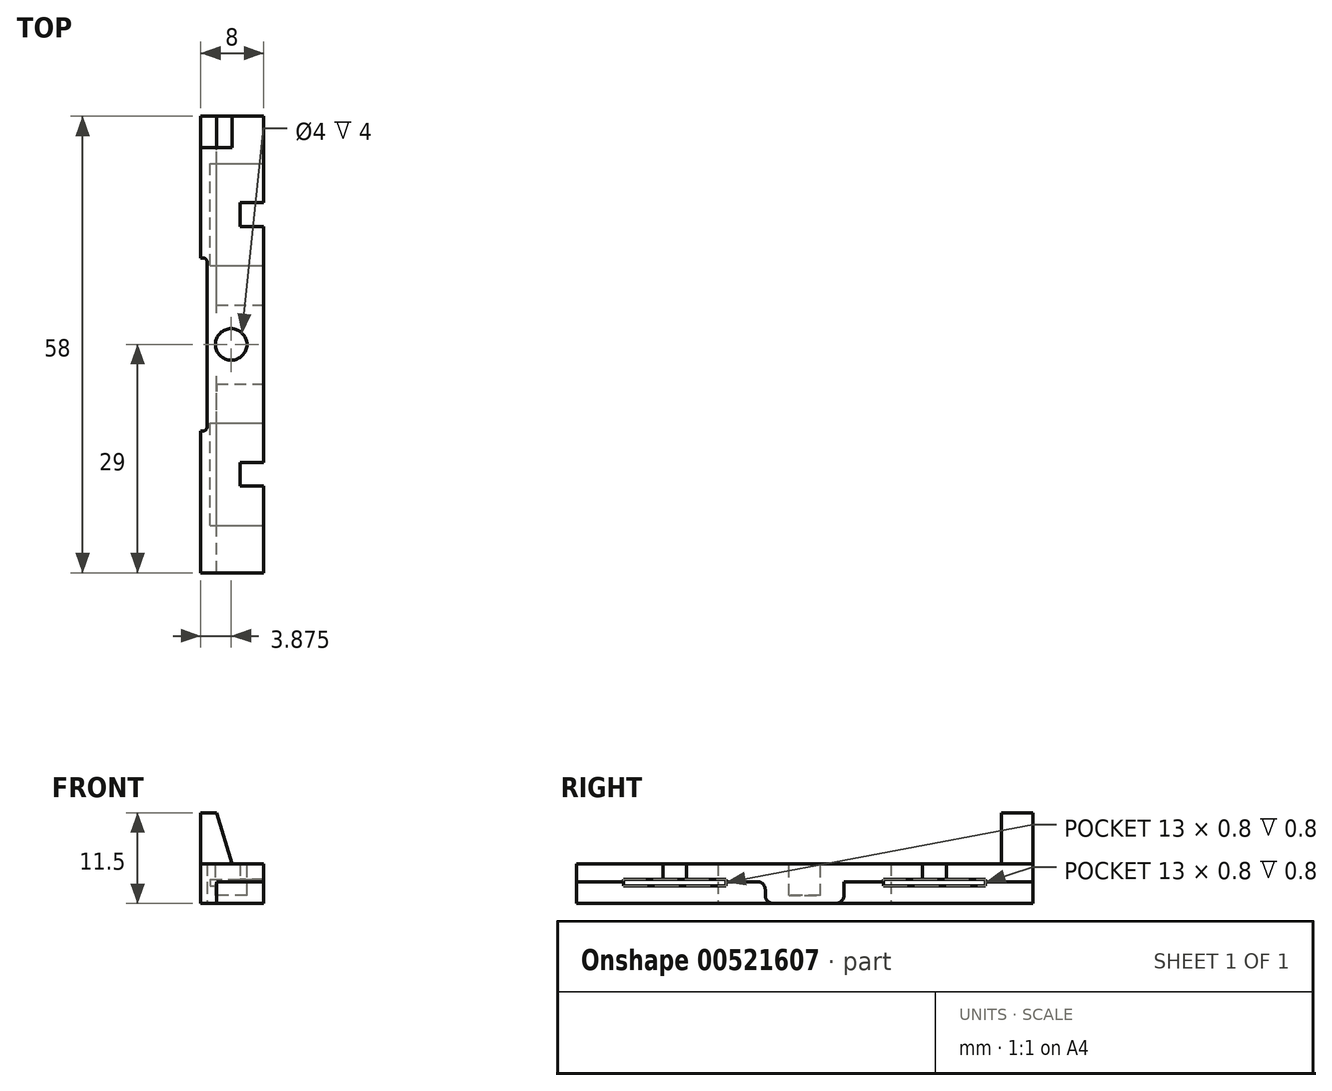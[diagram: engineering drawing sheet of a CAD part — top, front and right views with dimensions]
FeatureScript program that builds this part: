
annotation { "Feature Type Name" : "Feature", "Feature Type Description" : "" }
export const myFeature = defineFeature(function(context is Context, id is Id, definition is map)
    precondition{}
    {
        {
            var Q0;
            Q0=qCreatedBy(makeId("Right.planeOp"),FACE);
            var sketch = newSketch(context, id + "F0", { "sketchPlane" : qUnion([Q0])});
            skLineSegment(sketch, "E0.bottom", {"start": v(-29, 2.5) * mm, "end": v(29, 2.5) * mm});
            skLineSegment(sketch, "E0.top", {"start": v(-29, -2.5) * mm, "end": v(29, -2.5) * mm});
            skLineSegment(sketch, "E0.left", {"start": v(-29, 2.5) * mm, "end": v(-29, -2.5) * mm});
            skLineSegment(sketch, "E0.right", {"start": v(29, 2.5) * mm, "end": v(29, -2.5) * mm});
            skPoint(sketch, "E0.middle", {"position": v(0, 0) * mm});
            skSolve(sketch);
        }
        {
            var Q0;
            Q0 = qSketchRegion(id + "F0", true);
            extrude(context, id + "F1", {"entities" : qUnion([Q0]), "depth" : 2 * mm, "offsetDistance" : 25 * mm});
        }
        {
            var Q0;
            Q0=makeQuery(id+"F1.opExtrude","CAP_FACE",FACE,{"disambiguationData":[OSD([sQuery(id+"F0.wireOp",EDGE,"E0.bottom"),sQuery(id+"F0.wireOp",EDGE,"E0.top"),sQuery(id+"F0.wireOp",EDGE,"E0.left"),sQuery(id+"F0.wireOp",EDGE,"E0.right")])],"isStart":false});
            var sketch = newSketch(context, id + "F2", { "sketchPlane" : qUnion([Q0])});
            skLineSegment(sketch, "E1.bottom", {"start": v(10, 0.25) * mm, "end": v(23, 0.25) * mm});
            skLineSegment(sketch, "E1.top", {"start": v(10, -0.25) * mm, "end": v(23, -0.25) * mm});
            skLineSegment(sketch, "E1.left", {"start": v(10, 0.25) * mm, "end": v(10, -0.25) * mm});
            skLineSegment(sketch, "E1.right", {"start": v(23, 0.25) * mm, "end": v(23, -0.25) * mm});
            skPoint(sketch, "E1.middle", {"position": v(16.5, 0) * mm});
            skLineSegment(sketch, "E2.bottom", {"start": v(-23, 0.25) * mm, "end": v(-10, 0.25) * mm});
            skLineSegment(sketch, "E2.top", {"start": v(-23, -0.25) * mm, "end": v(-10, -0.25) * mm});
            skLineSegment(sketch, "E2.left", {"start": v(-23, 0.25) * mm, "end": v(-23, -0.25) * mm});
            skLineSegment(sketch, "E2.right", {"start": v(-10, 0.25) * mm, "end": v(-10, -0.25) * mm});
            skPoint(sketch, "E2.middle", {"position": v(-16.5, 0) * mm});
            skSolve(sketch);
        }
        {
            var Q0;
            Q0 = qSketchRegion(id + "F2", true);
            extrude(context, id + "F3", {"entities" : qUnion([Q0]), "operationType" : NewBodyOperationType.REMOVE, "oppositeDirection" : true, "depth" : .8 * mm, "offsetDistance" : 25 * mm});
        }
        {
            var Q0;
            Q0=makeQuery(id+"F1.opExtrude","CAP_FACE",FACE,{"disambiguationData":[OSD([sQuery(id+"F0.wireOp",EDGE,"E0.bottom"),sQuery(id+"F0.wireOp",EDGE,"E0.top"),sQuery(id+"F0.wireOp",EDGE,"E0.left"),sQuery(id+"F0.wireOp",EDGE,"E0.right")])],"isStart":false});
            var sketch = newSketch(context, id + "F4", { "sketchPlane" : qUnion([Q0])});
            skPoint(sketch, "E3.oppositeSnap0", {"position": v(-16.5, 0.25) * mm});
            skLineSegment(sketch, "E3.bottom", {"start": v(-29, 2.5) * mm, "end": v(29, 2.5) * mm});
            skLineSegment(sketch, "E3.top", {"start": v(-29, 0.25) * mm, "end": v(29, 0.25) * mm});
            skLineSegment(sketch, "E3.left", {"start": v(-29, 2.5) * mm, "end": v(-29, 0.25) * mm});
            skLineSegment(sketch, "E3.right", {"start": v(29, 2.5) * mm, "end": v(29, 0.25) * mm});
            skSolve(sketch);
        }
        {
            var Q0;
            Q0 = qSketchRegion(id + "F4", true);
            extrude(context, id + "F5", {"entities" : qUnion([Q0]), "operationType" : NewBodyOperationType.ADD, "depth" : 6 * mm, "offsetDistance" : 25 * mm});
        }
        {
            var Q0;
            Q0=makeQuery(id+"F5.boolean.opBoolean","MERGE",FACE,{"derivedFrom":[makeQuery(id+"F3.boolean.opBoolean","COPY",FACE,{"derivedFrom":makeQuery(id+"F3.opExtrude","SWEPT_FACE",FACE,{"disambiguationData":[OSD([sQuery(id+"F2.wireOp",EDGE,"E1.bottom")])]})}),makeQuery(id+"F3.boolean.opBoolean","COPY",FACE,{"derivedFrom":makeQuery(id+"F3.opExtrude","SWEPT_FACE",FACE,{"disambiguationData":[OSD([sQuery(id+"F2.wireOp",EDGE,"E2.bottom")])]})}),makeQuery(id+"F5.opExtrude","SWEPT_FACE",FACE,{"disambiguationData":[OSD([sQuery(id+"F4.wireOp",EDGE,"E3.top")])]})]});
            var sketch = newSketch(context, id + "F6", { "sketchPlane" : qUnion([Q0])});
            skLineSegment(sketch, "E4.bottom", {"start": v(2, 5) * mm, "end": v(8, 5) * mm});
            skLineSegment(sketch, "E4.top", {"start": v(2, -5) * mm, "end": v(8, -5) * mm});
            skLineSegment(sketch, "E4.left", {"start": v(2, 5) * mm, "end": v(2, -5) * mm});
            skLineSegment(sketch, "E4.right", {"start": v(8, 5) * mm, "end": v(8, -5) * mm});
            skPoint(sketch, "E4.middle", {"position": v(5, 0) * mm});
            skSolve(sketch);
        }
        {
            var Q0;
            Q0=makeQuery(id+"F6.imprint","IMPRINT",FACE,{"disambiguationData":[TD([[makeQuery(id+"F6.imprint","IMPRINT",EDGE,{"derivedFrom":sQuery(id+"F6.wireOp",EDGE,"E4.bottom")}),-1.0]])]});
            var Q1;
            Q1=makeQuery(id+"F1.opExtrude","SWEPT_FACE",FACE,{"disambiguationData":[OSD([sQuery(id+"F0.wireOp",EDGE,"E0.top")])]});
            extrude(context, id + "F7", {"entities" : qUnion([Q0]), "operationType" : NewBodyOperationType.ADD, "endBound" : BoundingType.UP_TO_SURFACE, "depth" : 25 * mm, "endBoundEntityFace" : qUnion([Q1]), "offsetDistance" : 25 * mm});
        }
        {
            var Q0;
            Q0=makeQuery(id+"F5.boolean.opBoolean","MERGE",FACE,{"derivedFrom":[makeQuery(id+"F1.opExtrude","SWEPT_FACE",FACE,{"disambiguationData":[OSD([sQuery(id+"F0.wireOp",EDGE,"E0.bottom")])]}),makeQuery(id+"F5.opExtrude","SWEPT_FACE",FACE,{"disambiguationData":[OSD([sQuery(id+"F4.wireOp",EDGE,"E3.bottom")])]})]});
            var sketch = newSketch(context, id + "F8", { "sketchPlane" : qUnion([Q0])});
            skCircle(sketch, "E5", {"center": v(3.88, 0) * mm, "radius": 2 * mm});
            skSolve(sketch);
        }
        {
            var Q0;
            Q0 = qSketchRegion(id + "F8", true);
            extrude(context, id + "F9", {"entities" : qUnion([Q0]), "operationType" : NewBodyOperationType.REMOVE, "oppositeDirection" : true, "depth" : 4 * mm, "offsetDistance" : 25 * mm});
        }
        {
            var Q0;
            Q0=makeQuery(id+"F7.opExtrude","CAP_EDGE",EDGE,{"disambiguationData":[OSD([sQuery(id+"F6.wireOp",EDGE,"E4.bottom")])],"isStart":false});
            var Q1;
            Q1=makeQuery(id+"F7.opExtrude","CAP_EDGE",EDGE,{"disambiguationData":[OSD([sQuery(id+"F6.wireOp",EDGE,"E4.bottom")])],"isStart":true});
            var Q2;
            Q2=makeQuery(id+"F7.opExtrude","CAP_EDGE",EDGE,{"disambiguationData":[OSD([sQuery(id+"F6.wireOp",EDGE,"E4.top")])],"isStart":true});
            var Q3;
            Q3=makeQuery(id+"F7.opExtrude","CAP_EDGE",EDGE,{"disambiguationData":[OSD([sQuery(id+"F6.wireOp",EDGE,"E4.top")])],"isStart":false});
            fillet(context, id + "F10", {"entities" : qUnion([Q0, Q1, Q2, Q3]), "radius" : 1 * mm, "tangentPropagation" : true, "allowEdgeOverflow" : false});
        }
        {
            var Q0;
            Q0=makeQuery(id+"F5.boolean.opBoolean","MERGE",FACE,{"derivedFrom":[makeQuery(id+"F1.opExtrude","SWEPT_FACE",FACE,{"disambiguationData":[OSD([sQuery(id+"F0.wireOp",EDGE,"E0.right")])]}),makeQuery(id+"F5.opExtrude","SWEPT_FACE",FACE,{"disambiguationData":[OSD([sQuery(id+"F4.wireOp",EDGE,"E3.right")])]})]});
            var sketch = newSketch(context, id + "F11", { "sketchPlane" : qUnion([Q0])});
            skLineSegment(sketch, "E6", {"start": v(0, 2.5) * mm, "end": v(0, 9) * mm});
            skLineSegment(sketch, "E7", {"start": v(0, 9) * mm, "end": v(-2, 9) * mm});
            skLineSegment(sketch, "E8", {"start": v(-2, 9) * mm, "end": v(-4, 2.5) * mm});
            skLineSegment(sketch, "E9", {"start": v(-4, 2.5) * mm, "end": v(0, 2.5) * mm});
            skSolve(sketch);
        }
        {
            var Q0;
            Q0=makeQuery(id+"F11.imprint","IMPRINT",FACE,{"disambiguationData":[TD([[makeQuery(id+"F11.imprint","IMPRINT",EDGE,{"derivedFrom":sQuery(id+"F11.wireOp",EDGE,"E6")}),1.0]])]});
            extrude(context, id + "F12", {"entities" : qUnion([Q0]), "operationType" : NewBodyOperationType.ADD, "oppositeDirection" : true, "depth" : 4 * mm, "offsetDistance" : 25 * mm});
        }
        {
            var Q0;
            {var subQ0=sQuery(id+"F11.wireOp",EDGE,"E6");Q0=makeQuery(id+"Fv3bD8ehhflkk99_1.1.F12.boolean.opBoolean","MERGE",FACE,{"derivedFrom":[makeQuery(id+"F12.boolean.opBoolean","MERGE",FACE,{"derivedFrom":[makeQuery(id+"F1.opExtrude","CAP_FACE",FACE,{"disambiguationData":[OSD([sQuery(id+"F0.wireOp",EDGE,"E0.bottom"),sQuery(id+"F0.wireOp",EDGE,"E0.top"),sQuery(id+"F0.wireOp",EDGE,"E0.left"),sQuery(id+"F0.wireOp",EDGE,"E0.right")])],"isStart":true}),makeQuery(id+"F12.opExtrude","SWEPT_FACE",FACE,{"disambiguationData":[OSD([subQ0])]})]}),makeQuery(id+"Fv3bD8ehhflkk99_1.1.F12.opExtrude","SWEPT_FACE",FACE,{"disambiguationData":[OSD([subQ0])]})]});}
            var sketch = newSketch(context, id + "F13", { "sketchPlane" : qUnion([Q0])});
            skLineSegment(sketch, "E10.bottom", {"start": v(-11, 2.5) * mm, "end": v(11, 2.5) * mm});
            skLineSegment(sketch, "E10.top", {"start": v(-11, -2.5) * mm, "end": v(11, -2.5) * mm});
            skLineSegment(sketch, "E10.left", {"start": v(-11, 2.5) * mm, "end": v(-11, -2.5) * mm});
            skLineSegment(sketch, "E10.right", {"start": v(11, 2.5) * mm, "end": v(11, -2.5) * mm});
            skPoint(sketch, "E10.middle", {"position": v(0, 0) * mm});
            skSolve(sketch);
        }
        {
            var Q0;
            Q0=makeQuery(id+"F13.imprint","IMPRINT",FACE,{"disambiguationData":[TD([[makeQuery(id+"F13.imprint","IMPRINT",EDGE,{"derivedFrom":sQuery(id+"F13.wireOp",EDGE,"E10.bottom")}),1.0]])]});
            extrude(context, id + "F14", {"entities" : qUnion([Q0]), "operationType" : NewBodyOperationType.REMOVE, "oppositeDirection" : true, "depth" : .8 * mm, "offsetDistance" : 25 * mm});
        }
        {
            var Q0;
            {var subQ0=sQuery(id+"F0.wireOp",EDGE,"E0.top");var subQ1=sQuery(id+"F13.wireOp",EDGE,"E10.left");Q0=makeQuery(id+"F14.boolean.opBoolean","COPY",EDGE,{"disambiguationData":[TD([makeQuery(id+"F1.opExtrude","SWEPT_FACE",FACE,{"disambiguationData":[OSD([subQ0])]})])],"derivedFrom":makeQuery(id+"F14.opExtrude","CAP_EDGE",EDGE,{"disambiguationData":[OSD([subQ1])],"isStart":false})});}
            var Q1;
            {var subQ0=sQuery(id+"F13.wireOp",EDGE,"E10.left");Q1=makeQuery(id+"F14.boolean.opBoolean","COPY",EDGE,{"disambiguationData":[TD([makeQuery(id+"F1.opExtrude","SWEPT_FACE",FACE,{"disambiguationData":[OSD([sQuery(id+"F0.wireOp",EDGE,"E0.bottom")])]})])],"derivedFrom":makeQuery(id+"F14.opExtrude","CAP_EDGE",EDGE,{"disambiguationData":[OSD([subQ0])],"isStart":false})});}
            var Q2;
            {var subQ0=sQuery(id+"F13.wireOp",EDGE,"E10.right");Q2=makeQuery(id+"F14.boolean.opBoolean","COPY",EDGE,{"disambiguationData":[TD([makeQuery(id+"F1.opExtrude","SWEPT_FACE",FACE,{"disambiguationData":[OSD([sQuery(id+"F0.wireOp",EDGE,"E0.bottom")])]})])],"derivedFrom":makeQuery(id+"F14.opExtrude","CAP_EDGE",EDGE,{"disambiguationData":[OSD([subQ0])],"isStart":false})});}
            var Q3;
            {var subQ0=sQuery(id+"F0.wireOp",EDGE,"E0.top");var subQ1=sQuery(id+"F13.wireOp",EDGE,"E10.right");Q3=makeQuery(id+"F14.boolean.opBoolean","COPY",EDGE,{"disambiguationData":[TD([makeQuery(id+"F1.opExtrude","SWEPT_FACE",FACE,{"disambiguationData":[OSD([subQ0])]})])],"derivedFrom":makeQuery(id+"F14.opExtrude","CAP_EDGE",EDGE,{"disambiguationData":[OSD([subQ1])],"isStart":false})});}
            var Q4;
            Q4=makeQuery(id+"Fv3bD8ehhflkk99_1.1.F12.opExtrude","SWEPT_EDGE",EDGE,{"disambiguationData":[OSD([sQuery(id+"F0.wireOp",EDGE,"E0.bottom"),sQuery(id+"F0.wireOp",EDGE,"E0.right"),sQuery(id+"F4.wireOp",EDGE,"E3.bottom"),sQuery(id+"F4.wireOp",EDGE,"E3.right"),sQuery(id+"F11.wireOp",EDGE,"E8"),sQuery(id+"F11.wireOp",EDGE,"E9")])]});
            var Q5;
            Q5=makeQuery(id+"Fv3bD8ehhflkk99_1.1.F12.opExtrude","CAP_EDGE",EDGE,{"disambiguationData":[OSD([sQuery(id+"F11.wireOp",EDGE,"E9")])],"isStart":false});
            var Q6;
            Q6=makeQuery(id+"F12.opExtrude","SWEPT_EDGE",EDGE,{"disambiguationData":[OSD([sQuery(id+"F0.wireOp",EDGE,"E0.bottom"),sQuery(id+"F0.wireOp",EDGE,"E0.right"),sQuery(id+"F4.wireOp",EDGE,"E3.bottom"),sQuery(id+"F4.wireOp",EDGE,"E3.right"),sQuery(id+"F11.wireOp",EDGE,"E8"),sQuery(id+"F11.wireOp",EDGE,"E9")])]});
            var Q7;
            Q7=makeQuery(id+"F12.opExtrude","CAP_EDGE",EDGE,{"disambiguationData":[OSD([sQuery(id+"F11.wireOp",EDGE,"E9")])],"isStart":false});
            fillet(context, id + "F15", {"entities" : qUnion([Q0, Q1, Q2, Q3, Q4, Q5, Q6, Q7]), "radius" : .5 * mm, "tangentPropagation" : true, "allowEdgeOverflow" : false});
        }
        {
            var Q0;
            {var subQ2=sQuery(id+"F2.wireOp",EDGE,"E2.bottom");var subQ3=sQuery(id+"F0.wireOp",EDGE,"E0.left");var subQ5=sQuery(id+"F4.wireOp",EDGE,"E3.top");Q0=makeQuery(id+"F7.boolean.opBoolean","SPLIT",FACE,{"disambiguationData":[TD([makeQuery(id+"F1.opExtrude","SWEPT_FACE",FACE,{"disambiguationData":[OSD([subQ3])]})])],"derivedFrom":makeQuery(id+"F5.boolean.opBoolean","MERGE",FACE,{"derivedFrom":[makeQuery(id+"F3.boolean.opBoolean","COPY",FACE,{"derivedFrom":makeQuery(id+"F3.opExtrude","SWEPT_FACE",FACE,{"disambiguationData":[OSD([sQuery(id+"F2.wireOp",EDGE,"E1.bottom")])]})}),makeQuery(id+"F3.boolean.opBoolean","COPY",FACE,{"derivedFrom":makeQuery(id+"F3.opExtrude","SWEPT_FACE",FACE,{"disambiguationData":[OSD([subQ2])]})}),makeQuery(id+"F5.opExtrude","SWEPT_FACE",FACE,{"disambiguationData":[OSD([subQ5])]})]})});}
            var sketch = newSketch(context, id + "F16", { "sketchPlane" : qUnion([Q0])});
            skLineSegment(sketch, "E11.bottom", {"start": v(1.2, 23) * mm, "end": v(8, 23) * mm});
            skLineSegment(sketch, "E11.top", {"start": v(1.2, 10) * mm, "end": v(8, 10) * mm});
            skLineSegment(sketch, "E11.right", {"start": v(8, 23) * mm, "end": v(8, 10) * mm});
            skLineSegment(sketch, "E12.top", {"start": v(1.2, -23) * mm, "end": v(8, -23) * mm});
            skLineSegment(sketch, "E12.left", {"start": v(1.2, -10) * mm, "end": v(1.2, -23) * mm});
            skLineSegment(sketch, "E12.right", {"start": v(8, -10) * mm, "end": v(8, -23) * mm});
            skLineSegment(sketch, "E13", {"start": v(1.2, -10) * mm, "end": v(8, -10) * mm});
            skLineSegment(sketch, "E14", {"start": v(1.2, 23) * mm, "end": v(1.2, 10) * mm});
            skSolve(sketch);
        }
        {
            var Q0;
            Q0 = qSketchRegion(id + "F16", true);
            extrude(context, id + "F17", {"entities" : qUnion([Q0]), "operationType" : NewBodyOperationType.REMOVE, "oppositeDirection" : true, "depth" : .3 * mm, "offsetDistance" : 25 * mm});
        }
        {
            var Q0;
            Q0=makeQuery(id+"F17.boolean.opBoolean","COPY",FACE,{"derivedFrom":makeQuery(id+"F17.opExtrude","CAP_FACE",FACE,{"disambiguationData":[OSD([sQuery(id+"F16.wireOp",EDGE,"E12.top"),sQuery(id+"F16.wireOp",EDGE,"E12.left"),sQuery(id+"F16.wireOp",EDGE,"E12.right"),sQuery(id+"F16.wireOp",EDGE,"E13")])],"isStart":false})});
            var sketch = newSketch(context, id + "F18", { "sketchPlane" : qUnion([Q0])});
            skLineSegment(sketch, "E15.bottom", {"start": v(8, -15) * mm, "end": v(5, -15) * mm});
            skLineSegment(sketch, "E15.top", {"start": v(8, -18) * mm, "end": v(5, -18) * mm});
            skLineSegment(sketch, "E15.left", {"start": v(8, -15) * mm, "end": v(8, -18) * mm});
            skLineSegment(sketch, "E15.right", {"start": v(5, -15) * mm, "end": v(5, -18) * mm});
            skLineSegment(sketch, "E16.bottom", {"start": v(8, 18) * mm, "end": v(5, 18) * mm});
            skLineSegment(sketch, "E16.top", {"start": v(8, 15) * mm, "end": v(5, 15) * mm});
            skLineSegment(sketch, "E16.left", {"start": v(8, 18) * mm, "end": v(8, 15) * mm});
            skLineSegment(sketch, "E16.right", {"start": v(5, 18) * mm, "end": v(5, 15) * mm});
            skSolve(sketch);
        }
        {
            var Q0;
            Q0 = qSketchRegion(id + "F18", true);
            extrude(context, id + "F19", {"entities" : qUnion([Q0]), "operationType" : NewBodyOperationType.REMOVE, "endBound" : BoundingType.UP_TO_NEXT, "oppositeDirection" : true, "depth" : 25 * mm, "offsetDistance" : 25 * mm});
        }
    });
